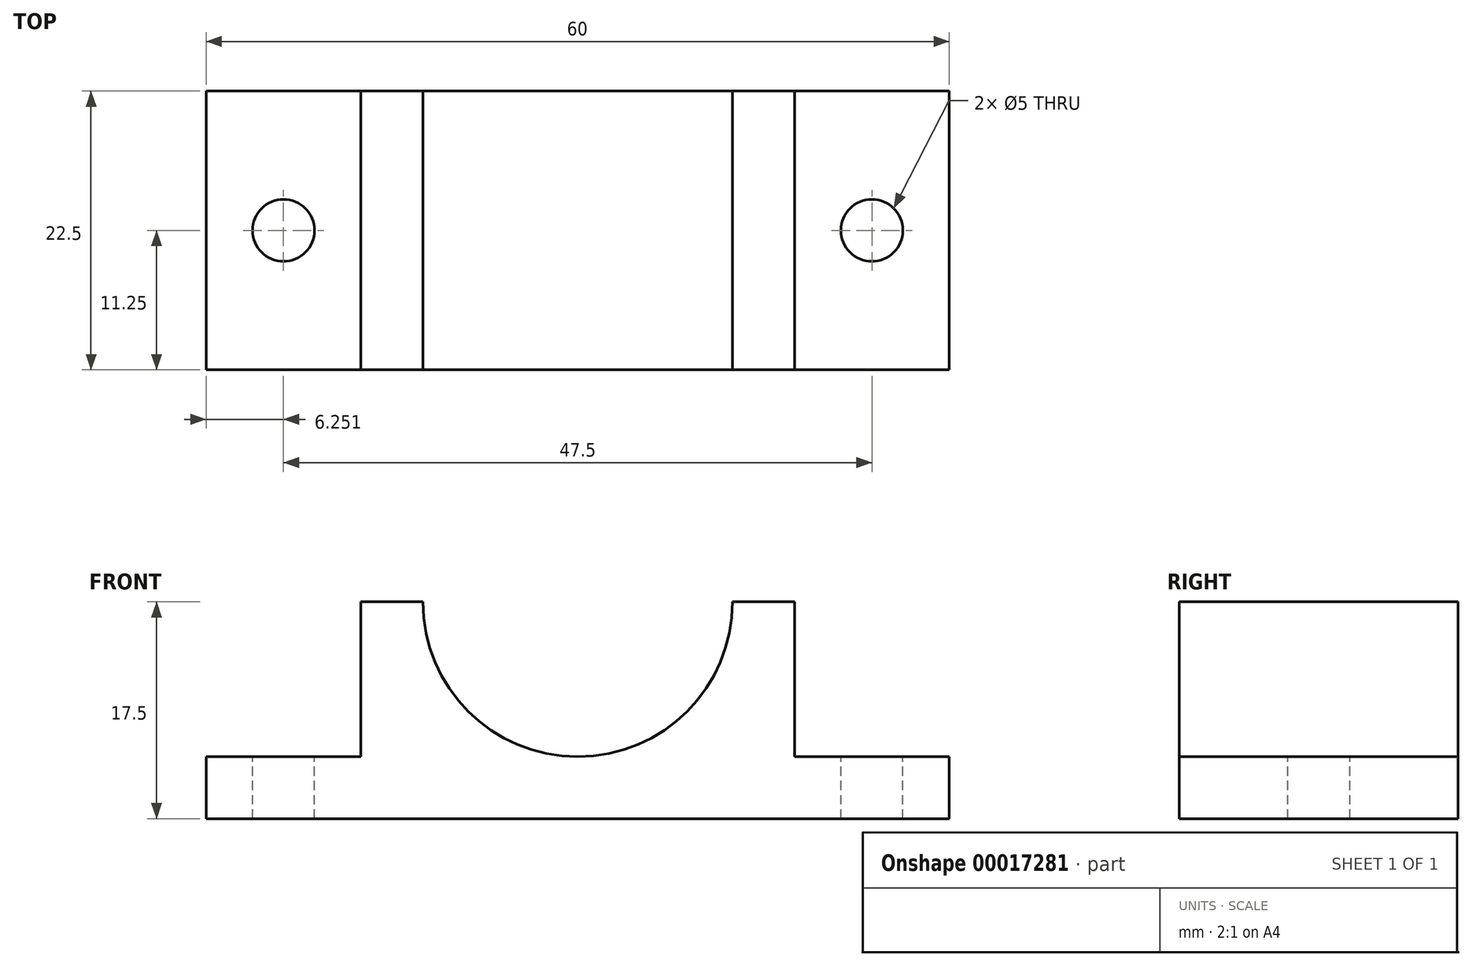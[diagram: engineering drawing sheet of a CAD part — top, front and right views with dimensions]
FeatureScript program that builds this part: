
annotation { "Feature Type Name" : "Feature", "Feature Type Description" : "" }
export const myFeature = defineFeature(function(context is Context, id is Id, definition is map)
    precondition{}
    {
        {
            var Q0;
            Q0=qCreatedBy(makeId("Front.planeOp"),FACE);
            var sketch = newSketch(context, id + "F0", { "sketchPlane" : qUnion([Q0])});
            skLineSegment(sketch, "E0", {"start": v(-38.85, 15.68) * mm, "end": v(21.15, 15.68) * mm});
            skLineSegment(sketch, "E1", {"start": v(-38.85, 15.68) * mm, "end": v(-38.85, 20.68) * mm});
            skLineSegment(sketch, "E2", {"start": v(21.15, 15.68) * mm, "end": v(21.15, 20.68) * mm});
            skLineSegment(sketch, "E3", {"start": v(21.15, 20.68) * mm, "end": v(8.65, 20.68) * mm});
            skLineSegment(sketch, "E4", {"start": v(-38.85, 20.68) * mm, "end": v(-26.35, 20.68) * mm});
            skLineSegment(sketch, "E5", {"start": v(-26.35, 20.68) * mm, "end": v(-26.35, 33.18) * mm});
            skLineSegment(sketch, "E6", {"start": v(8.65, 20.68) * mm, "end": v(8.65, 33.18) * mm});
            skArc(sketch, "E7", {"start": v(-21.35, 33.18) * mm, "mid": v(-8.85, 20.68) * mm, "end": v(3.65, 33.18) * mm});
            skLineSegment(sketch, "E8", {"start": v(-26.35, 33.18) * mm, "end": v(-21.35, 33.18) * mm});
            skLineSegment(sketch, "E9", {"start": v(8.65, 33.18) * mm, "end": v(3.65, 33.18) * mm});
            skSolve(sketch);
        }
        {
            var Q0;
            Q0=makeQuery(id+"F0.imprint","IMPRINT",FACE,{"disambiguationData":[TD([[makeQuery(id+"F0.imprint","IMPRINT",EDGE,{"derivedFrom":sQuery(id+"F0.wireOp",EDGE,"E0")}),1.0]])]});
            extrude(context, id + "F1", {"entities" : qUnion([Q0]), "depth" : 22.5 * mm});
        }
        {
            var Q0;
            Q0=makeQuery(id+"F1.opExtrude","SWEPT_FACE",FACE,{"disambiguationData":[OSD([sQuery(id+"F0.wireOp",EDGE,"E3")])]});
            var sketch = newSketch(context, id + "F2", { "sketchPlane" : qUnion([Q0])});
            skCircle(sketch, "E10", {"center": v(14.9, -11.25) * mm, "radius": 2.5 * mm});
            skCircle(sketch, "E11", {"center": v(-32.62, -11.2) * mm, "radius": 2.5 * mm});
            skSolve(sketch);
        }
        {
            var Q0;
            Q0=makeQuery(id+"F2.imprint","IMPRINT",FACE,{"disambiguationData":[TD([[makeQuery(id+"F2.imprint","IMPRINT",EDGE,{"derivedFrom":sQuery(id+"F2.wireOp",EDGE,"E10")}),1.0]])]});
            extrude(context, id + "F3", {"entities" : qUnion([Q0]), "operationType" : NewBodyOperationType.REMOVE, "oppositeDirection" : true, "depth" : 5 * mm});
        }
        {
            var Q0;
            Q0=makeQuery(id+"F1.opExtrude","SWEPT_FACE",FACE,{"disambiguationData":[OSD([sQuery(id+"F0.wireOp",EDGE,"E4")])]});
            var sketch = newSketch(context, id + "F4", { "sketchPlane" : qUnion([Q0])});
            skCircle(sketch, "E12", {"center": v(-32.6, -11.25) * mm, "radius": 2.5 * mm});
            skSolve(sketch);
        }
        {
            var Q0;
            Q0=makeQuery(id+"F4.imprint","IMPRINT",FACE,{"disambiguationData":[TD([[makeQuery(id+"F4.imprint","IMPRINT",EDGE,{"derivedFrom":sQuery(id+"F4.wireOp",EDGE,"E12")}),1.0]])]});
            extrude(context, id + "F5", {"entities" : qUnion([Q0]), "operationType" : NewBodyOperationType.REMOVE, "oppositeDirection" : true, "depth" : 5 * mm});
        }
    });
